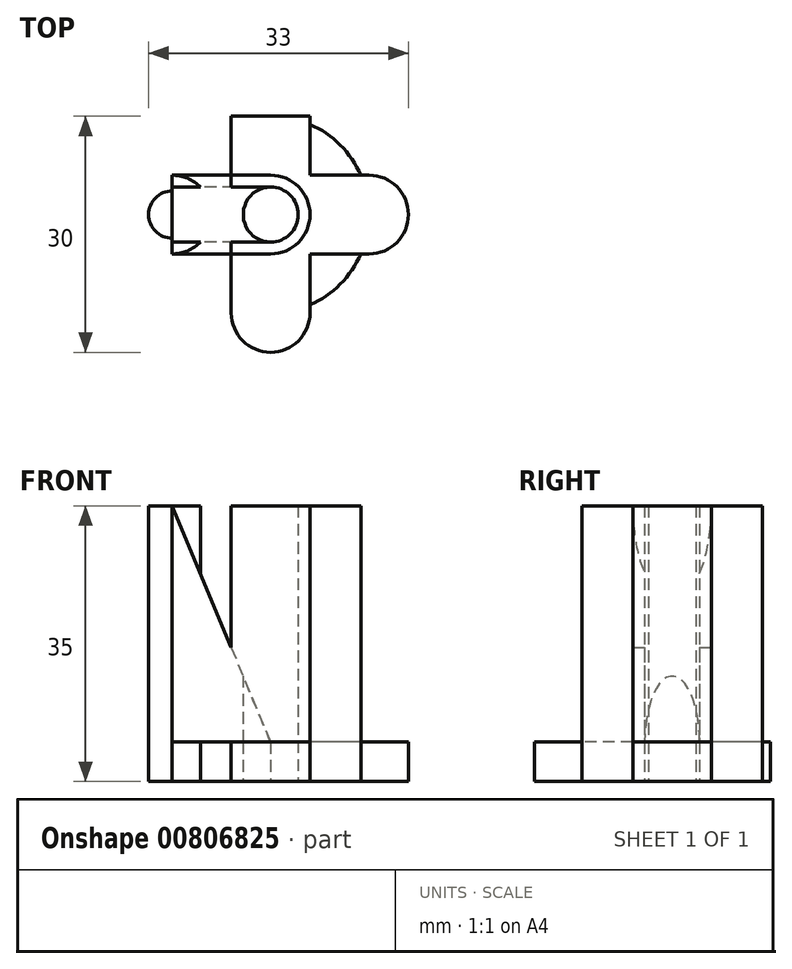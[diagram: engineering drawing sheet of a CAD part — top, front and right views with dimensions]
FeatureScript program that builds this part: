
annotation { "Feature Type Name" : "Feature", "Feature Type Description" : "" }
export const myFeature = defineFeature(function(context is Context, id is Id, definition is map)
    precondition{}
    {
        {
            var Q0;
            Q0=qCreatedBy(makeId("Top.planeOp"),FACE);
            var sketch = newSketch(context, id + "F0", { "sketchPlane" : qUnion([Q0])});
            skCircle(sketch, "E0", {"center": v(0, 0) * mm, "radius": 12.5 * mm});
            skCircle(sketch, "E1", {"center": v(0, 0) * mm, "radius": 3.5 * mm});
            skCircle(sketch, "E2", {"center": v(0, -12.5) * mm, "radius": 5 * mm});
            skCircle(sketch, "E3", {"center": v(0, 12.5) * mm, "radius": 5 * mm});
            skCircle(sketch, "E4", {"center": v(12.5, 0) * mm, "radius": 5 * mm});
            skCircle(sketch, "E5", {"center": v(-12.5, 0) * mm, "radius": 5 * mm});
            skCircle(sketch, "E6", {"center": v(-12.5, 0) * mm, "radius": 3 * mm});
            skCircle(sketch, "E7", {"center": v(0, 12.5) * mm, "radius": 3 * mm});
            skCircle(sketch, "E8", {"center": v(12.5, 0) * mm, "radius": 3 * mm});
            skCircle(sketch, "E9", {"center": v(0, -12.5) * mm, "radius": 3 * mm});
            skCircle(sketch, "E10", {"center": v(0, 0) * mm, "radius": 5 * mm});
            skLineSegment(sketch, "E11.bottom", {"start": v(0, 3.5) * mm, "end": v(-12.5, 3.5) * mm});
            skLineSegment(sketch, "E11.top", {"start": v(0, 5) * mm, "end": v(-12.5, 5) * mm});
            skLineSegment(sketch, "E11.left", {"start": v(0, 3.5) * mm, "end": v(0, 5) * mm});
            skLineSegment(sketch, "E11.right", {"start": v(-12.5, 3.5) * mm, "end": v(-12.5, 5) * mm});
            skLineSegment(sketch, "E12.bottom", {"start": v(0, -3.5) * mm, "end": v(-12.5, -3.5) * mm});
            skLineSegment(sketch, "E12.top", {"start": v(0, -5) * mm, "end": v(-12.5, -5) * mm});
            skLineSegment(sketch, "E12.left", {"start": v(0, -3.5) * mm, "end": v(0, -5) * mm});
            skLineSegment(sketch, "E12.right", {"start": v(-12.5, -3.5) * mm, "end": v(-12.5, -5) * mm});
            skLineSegment(sketch, "E13.bottom", {"start": v(5, 12.5) * mm, "end": v(-5, 12.5) * mm});
            skLineSegment(sketch, "E13.top", {"start": v(5, -12.5) * mm, "end": v(-5, -12.5) * mm});
            skLineSegment(sketch, "E13.left", {"start": v(5, 12.5) * mm, "end": v(5, -12.5) * mm});
            skLineSegment(sketch, "E13.right", {"start": v(-5, 12.5) * mm, "end": v(-5, -12.5) * mm});
            skLineSegment(sketch, "E14.bottom", {"start": v(12.5, 5) * mm, "end": v(-12.5, 5) * mm});
            skLineSegment(sketch, "E14.top", {"start": v(12.5, -5) * mm, "end": v(-12.5, -5) * mm});
            skLineSegment(sketch, "E14.left", {"start": v(12.5, 5) * mm, "end": v(12.5, -5) * mm});
            skLineSegment(sketch, "E14.right", {"start": v(-12.5, 5) * mm, "end": v(-12.5, -5) * mm});
            skSolve(sketch);
        }
        {
            var Q0;
            Q0=qCreatedBy(makeId("Front.planeOp"),FACE);
            var sketch = newSketch(context, id + "F1", { "sketchPlane" : qUnion([Q0])});
            skLineSegment(sketch, "E15", {"start": v(0, 0) * mm, "end": v(0, 10) * mm});
            skLineSegment(sketch, "E16", {"start": v(0, 10) * mm, "end": v(-12.5, 10) * mm});
            skLineSegment(sketch, "E17", {"start": v(-12.5, 10) * mm, "end": v(-12.5, 40) * mm});
            skLineSegment(sketch, "E18", {"start": v(-12.5, 40) * mm, "end": v(0, 10) * mm});
            skSolve(sketch);
        }
        {
            var Q0;
            Q0=makeQuery(id+"F1.imprint","IMPRINT",FACE,{"disambiguationData":[TD([[makeQuery(id+"F1.imprint","IMPRINT",EDGE,{"derivedFrom":sQuery(id+"F1.wireOp",EDGE,"E16")}),-1.0]])]});
            extrude(context, id + "F2", {"entities" : qUnion([Q0]), "endBound" : BoundingType.SYMMETRIC, "depth" : 10 * mm, "offsetDistance" : 25 * mm});
        }
        {
            var Q0;
            {var subQ0=sQuery(id+"F0.wireOp",EDGE,"E11.left");Q0=makeQuery(id+"F0.imprint","IMPRINT",FACE,{"disambiguationData":[TD([[makeQuery(id+"F0.imprint","IMPRINT",EDGE,{"derivedFrom":subQ0}),-1.0]])]});}
            var Q1;
            {var subQ0=sQuery(id+"F0.wireOp",EDGE,"E11.left");Q1=makeQuery(id+"F0.imprint","IMPRINT",FACE,{"disambiguationData":[TD([[makeQuery(id+"F0.imprint","IMPRINT",EDGE,{"derivedFrom":subQ0}),1.0]])]});}
            var Q2;
            {var subQ1=sQuery(id+"F0.wireOp",EDGE,"E10");var subQ3=sQuery(id+"F0.wireOp",EDGE,"E11.bottom");var subQ4=makeQuery(id+"F0.imprint","INTERSECT",VERTEX,{"derivedFrom":[subQ1,subQ3]});Q2=makeQuery(id+"F0.imprint","IMPRINT",FACE,{"disambiguationData":[TD([[makeQuery(id+"F0.imprint","IMPRINT",EDGE,{"disambiguationData":[TD([[subQ4,-1.0]])],"derivedFrom":subQ3}),-1.0]])]});}
            var Q3;
            {var subQ3=sQuery(id+"F0.wireOp",EDGE,"E14.bottom");var subQ7=sQuery(id+"F0.wireOp",EDGE,"E0");var subQ9=makeQuery(id+"F0.imprint","INTERSECT",VERTEX,{"disambiguationData":[OD(1.0)],"derivedFrom":[subQ7,subQ3]});Q3=makeQuery(id+"F0.imprint","IMPRINT",FACE,{"disambiguationData":[TD([[makeQuery(id+"F0.imprint","IMPRINT",EDGE,{"disambiguationData":[TD([[subQ9,-1.0]])],"derivedFrom":subQ7}),1.0]])]});}
            var Q4;
            {var subQ0=sQuery(id+"F0.wireOp",EDGE,"E5");var subQ1=sQuery(id+"F0.wireOp",EDGE,"E0");var subQ2=makeQuery(id+"F0.imprint","INTERSECT",VERTEX,{"disambiguationData":[OD(0.0)],"derivedFrom":[subQ1,subQ0]});Q4=makeQuery(id+"F0.imprint","IMPRINT",FACE,{"disambiguationData":[TD([[makeQuery(id+"F0.imprint","IMPRINT",EDGE,{"disambiguationData":[TD([[subQ2,-1.0]])],"derivedFrom":subQ1}),1.0]])]});}
            var Q5;
            {var subQ0=sQuery(id+"F0.wireOp",EDGE,"E5");var subQ1=sQuery(id+"F0.wireOp",EDGE,"E0");var subQ2=makeQuery(id+"F0.imprint","INTERSECT",VERTEX,{"disambiguationData":[OD(0.0)],"derivedFrom":[subQ1,subQ0]});Q5=makeQuery(id+"F0.imprint","IMPRINT",FACE,{"disambiguationData":[TD([[makeQuery(id+"F0.imprint","IMPRINT",EDGE,{"disambiguationData":[TD([[subQ2,-1.0]])],"derivedFrom":subQ1}),-1.0]])]});}
            var Q6;
            {var subQ0=sQuery(id+"F0.wireOp",EDGE,"E12.bottom");var subQ1=sQuery(id+"F0.wireOp",EDGE,"E0");var subQ2=makeQuery(id+"F0.imprint","INTERSECT",VERTEX,{"derivedFrom":[subQ1,subQ0]});Q6=makeQuery(id+"F0.imprint","IMPRINT",FACE,{"disambiguationData":[TD([[makeQuery(id+"F0.imprint","IMPRINT",EDGE,{"disambiguationData":[TD([[subQ2,-1.0]])],"derivedFrom":subQ1}),-1.0]])]});}
            var Q7;
            {var subQ0=sQuery(id+"F0.wireOp",EDGE,"E12.bottom");var subQ1=sQuery(id+"F0.wireOp",EDGE,"E0");var subQ2=makeQuery(id+"F0.imprint","INTERSECT",VERTEX,{"derivedFrom":[subQ1,subQ0]});Q7=makeQuery(id+"F0.imprint","IMPRINT",FACE,{"disambiguationData":[TD([[makeQuery(id+"F0.imprint","IMPRINT",EDGE,{"disambiguationData":[TD([[subQ2,-1.0]])],"derivedFrom":subQ1}),1.0]])]});}
            var Q8;
            {var subQ5=sQuery(id+"F0.wireOp",EDGE,"E14.top");var subQ7=sQuery(id+"F0.wireOp",EDGE,"E0");var subQ9=makeQuery(id+"F0.imprint","INTERSECT",VERTEX,{"disambiguationData":[OD(0.0)],"derivedFrom":[subQ7,subQ5]});Q8=makeQuery(id+"F0.imprint","IMPRINT",FACE,{"disambiguationData":[TD([[makeQuery(id+"F0.imprint","IMPRINT",EDGE,{"disambiguationData":[TD([[subQ9,1.0]])],"derivedFrom":subQ7}),1.0]])]});}
            var Q9;
            {var subQ1=sQuery(id+"F0.wireOp",EDGE,"E10");var subQ3=sQuery(id+"F0.wireOp",EDGE,"E12.bottom");var subQ4=makeQuery(id+"F0.imprint","INTERSECT",VERTEX,{"derivedFrom":[subQ1,subQ3]});Q9=makeQuery(id+"F0.imprint","IMPRINT",FACE,{"disambiguationData":[TD([[makeQuery(id+"F0.imprint","IMPRINT",EDGE,{"disambiguationData":[TD([[subQ4,-1.0]])],"derivedFrom":subQ3}),1.0]])]});}
            var Q10;
            {var subQ0=sQuery(id+"F0.wireOp",EDGE,"E12.left");Q10=makeQuery(id+"F0.imprint","IMPRINT",FACE,{"disambiguationData":[TD([[makeQuery(id+"F0.imprint","IMPRINT",EDGE,{"derivedFrom":subQ0}),-1.0]])]});}
            var Q11;
            {var subQ0=sQuery(id+"F0.wireOp",EDGE,"E14.top");var subQ1=sQuery(id+"F0.wireOp",EDGE,"E0");var subQ2=makeQuery(id+"F0.imprint","INTERSECT",VERTEX,{"disambiguationData":[OD(0.0)],"derivedFrom":[subQ1,subQ0]});Q11=makeQuery(id+"F0.imprint","IMPRINT",FACE,{"disambiguationData":[TD([[makeQuery(id+"F0.imprint","IMPRINT",EDGE,{"disambiguationData":[TD([[subQ2,1.0]])],"derivedFrom":subQ1}),-1.0]])]});}
            var Q12;
            {var subQ0=sQuery(id+"F0.wireOp",EDGE,"E14.bottom");var subQ1=sQuery(id+"F0.wireOp",EDGE,"E0");var subQ2=makeQuery(id+"F0.imprint","INTERSECT",VERTEX,{"disambiguationData":[OD(1.0)],"derivedFrom":[subQ1,subQ0]});Q12=makeQuery(id+"F0.imprint","IMPRINT",FACE,{"disambiguationData":[TD([[makeQuery(id+"F0.imprint","IMPRINT",EDGE,{"disambiguationData":[TD([[subQ2,-1.0]])],"derivedFrom":subQ1}),-1.0]])]});}
            var Q13;
            {var subQ0=sQuery(id+"F0.wireOp",EDGE,"E14.right");var subQ4=makeQuery(id+"F0.imprint","INTERSECT",VERTEX,{"derivedFrom":[sQuery(id+"F0.wireOp",EDGE,"E0"),subQ0]});Q13=makeQuery(id+"F0.imprint","IMPRINT",FACE,{"disambiguationData":[TD([[makeQuery(id+"F0.imprint","IMPRINT",EDGE,{"disambiguationData":[TD([[subQ4,1.0]])],"derivedFrom":subQ0}),-1.0]])]});}
            var Q14;
            {var subQ0=sQuery(id+"F0.wireOp",EDGE,"E14.right");var subQ1=sQuery(id+"F0.wireOp",EDGE,"E5");var subQ2=makeQuery(id+"F0.imprint","INTERSECT",VERTEX,{"derivedFrom":[subQ1,sQuery(id+"F0.wireOp",EDGE,"E14.bottom"),subQ0]});Q14=makeQuery(id+"F0.imprint","IMPRINT",FACE,{"disambiguationData":[TD([[makeQuery(id+"F0.imprint","IMPRINT",EDGE,{"disambiguationData":[TD([[subQ2,-1.0]])],"derivedFrom":subQ1}),1.0]])]});}
            extrude(context, id + "F3", {"entities" : qUnion([Q0, Q1, Q2, Q3, Q4, Q5, Q6, Q7, Q8, Q9, Q10, Q11, Q12, Q13, Q14]), "operationType" : NewBodyOperationType.ADD, "depth" : 40 * mm, "offsetDistance" : 25 * mm});
        }
        {
            var Q0;
            {var subQ0=sQuery(id+"F0.wireOp",EDGE,"E11.bottom");var subQ3=sQuery(id+"F0.wireOp",EDGE,"E10");var subQ4=makeQuery(id+"F0.imprint","INTERSECT",VERTEX,{"derivedFrom":[subQ3,subQ0]});Q0=makeQuery(id+"F0.imprint","IMPRINT",FACE,{"disambiguationData":[TD([[makeQuery(id+"F0.imprint","IMPRINT",EDGE,{"disambiguationData":[TD([[subQ4,-1.0]])],"derivedFrom":subQ3}),1.0]])]});}
            var Q1;
            {var subQ0=sQuery(id+"F0.wireOp",EDGE,"E11.bottom");var subQ1=sQuery(id+"F0.wireOp",EDGE,"E10");var subQ2=makeQuery(id+"F0.imprint","INTERSECT",VERTEX,{"derivedFrom":[subQ1,subQ0]});Q1=makeQuery(id+"F0.imprint","IMPRINT",FACE,{"disambiguationData":[TD([[makeQuery(id+"F0.imprint","IMPRINT",EDGE,{"disambiguationData":[TD([[subQ2,-1.0]])],"derivedFrom":subQ1}),-1.0]])]});}
            var Q2;
            {var subQ0=sQuery(id+"F0.wireOp",EDGE,"E13.right");var subQ1=sQuery(id+"F0.wireOp",EDGE,"E10");var subQ2=makeQuery(id+"F0.imprint","INTERSECT",VERTEX,{"derivedFrom":[subQ1,subQ0]});Q2=makeQuery(id+"F0.imprint","IMPRINT",FACE,{"disambiguationData":[TD([[makeQuery(id+"F0.imprint","IMPRINT",EDGE,{"disambiguationData":[TD([[subQ2,-1.0]])],"derivedFrom":subQ1}),-1.0]])]});}
            var Q3;
            {var subQ2=sQuery(id+"F0.wireOp",EDGE,"E11.bottom");var subQ5=sQuery(id+"F0.wireOp",EDGE,"E5");var subQ8=makeQuery(id+"F0.imprint","INTERSECT",VERTEX,{"derivedFrom":[subQ5,subQ2]});Q3=makeQuery(id+"F0.imprint","IMPRINT",FACE,{"disambiguationData":[TD([[makeQuery(id+"F0.imprint","IMPRINT",EDGE,{"disambiguationData":[TD([[subQ8,1.0]])],"derivedFrom":subQ5}),-1.0]])]});}
            var Q4;
            {var subQ0=sQuery(id+"F0.wireOp",EDGE,"E11.bottom");var subQ6=sQuery(id+"F0.wireOp",EDGE,"E0");var subQ10=makeQuery(id+"F0.imprint","INTERSECT",VERTEX,{"derivedFrom":[subQ6,subQ0]});Q4=makeQuery(id+"F0.imprint","IMPRINT",FACE,{"disambiguationData":[TD([[makeQuery(id+"F0.imprint","IMPRINT",EDGE,{"disambiguationData":[TD([[subQ10,-1.0]])],"derivedFrom":subQ6}),1.0]])]});}
            var Q5;
            {var subQ0=sQuery(id+"F0.wireOp",EDGE,"E6");var subQ1=sQuery(id+"F0.wireOp",EDGE,"E0");var subQ2=makeQuery(id+"F0.imprint","INTERSECT",VERTEX,{"disambiguationData":[OD(0.0)],"derivedFrom":[subQ1,subQ0]});Q5=makeQuery(id+"F0.imprint","IMPRINT",FACE,{"disambiguationData":[TD([[makeQuery(id+"F0.imprint","IMPRINT",EDGE,{"disambiguationData":[TD([[subQ2,-1.0]])],"derivedFrom":subQ1}),1.0]])]});}
            var Q6;
            {var subQ0=sQuery(id+"F0.wireOp",EDGE,"E6");var subQ1=sQuery(id+"F0.wireOp",EDGE,"E0");var subQ2=makeQuery(id+"F0.imprint","INTERSECT",VERTEX,{"disambiguationData":[OD(0.0)],"derivedFrom":[subQ1,subQ0]});Q6=makeQuery(id+"F0.imprint","IMPRINT",FACE,{"disambiguationData":[TD([[makeQuery(id+"F0.imprint","IMPRINT",EDGE,{"disambiguationData":[TD([[subQ2,-1.0]])],"derivedFrom":subQ1}),-1.0]])]});}
            var Q7;
            {var subQ0=sQuery(id+"F0.wireOp",EDGE,"E14.right");var subQ1=sQuery(id+"F0.wireOp",EDGE,"E0");var subQ2=makeQuery(id+"F0.imprint","INTERSECT",VERTEX,{"derivedFrom":[subQ1,subQ0]});Q7=makeQuery(id+"F0.imprint","IMPRINT",FACE,{"disambiguationData":[TD([[makeQuery(id+"F0.imprint","IMPRINT",EDGE,{"disambiguationData":[TD([[subQ2,-1.0]])],"derivedFrom":subQ1}),-1.0]])]});}
            var Q8;
            {var subQ0=sQuery(id+"F0.wireOp",EDGE,"E13.left");var subQ1=sQuery(id+"F0.wireOp",EDGE,"E0");var subQ2=makeQuery(id+"F0.imprint","INTERSECT",VERTEX,{"disambiguationData":[OD(0.0)],"derivedFrom":[subQ1,subQ0]});Q8=makeQuery(id+"F0.imprint","IMPRINT",FACE,{"disambiguationData":[TD([[makeQuery(id+"F0.imprint","IMPRINT",EDGE,{"disambiguationData":[TD([[subQ2,-1.0]])],"derivedFrom":subQ1}),1.0]])]});}
            var Q9;
            {var subQ0=sQuery(id+"F0.wireOp",EDGE,"E3");var subQ1=sQuery(id+"F0.wireOp",EDGE,"E0");var subQ2=makeQuery(id+"F0.imprint","INTERSECT",VERTEX,{"disambiguationData":[OD(0.0)],"derivedFrom":[subQ1,subQ0]});Q9=makeQuery(id+"F0.imprint","IMPRINT",FACE,{"disambiguationData":[TD([[makeQuery(id+"F0.imprint","IMPRINT",EDGE,{"disambiguationData":[TD([[subQ2,-1.0]])],"derivedFrom":subQ1}),1.0]])]});}
            var Q10;
            {var subQ0=sQuery(id+"F0.wireOp",EDGE,"E7");var subQ1=sQuery(id+"F0.wireOp",EDGE,"E0");var subQ2=makeQuery(id+"F0.imprint","INTERSECT",VERTEX,{"disambiguationData":[OD(0.0)],"derivedFrom":[subQ1,subQ0]});Q10=makeQuery(id+"F0.imprint","IMPRINT",FACE,{"disambiguationData":[TD([[makeQuery(id+"F0.imprint","IMPRINT",EDGE,{"disambiguationData":[TD([[subQ2,-1.0]])],"derivedFrom":subQ1}),1.0]])]});}
            var Q11;
            {var subQ0=sQuery(id+"F0.wireOp",EDGE,"E7");var subQ1=sQuery(id+"F0.wireOp",EDGE,"E0");var subQ2=makeQuery(id+"F0.imprint","INTERSECT",VERTEX,{"disambiguationData":[OD(0.0)],"derivedFrom":[subQ1,subQ0]});Q11=makeQuery(id+"F0.imprint","IMPRINT",FACE,{"disambiguationData":[TD([[makeQuery(id+"F0.imprint","IMPRINT",EDGE,{"disambiguationData":[TD([[subQ2,-1.0]])],"derivedFrom":subQ1}),-1.0]])]});}
            var Q12;
            {var subQ0=sQuery(id+"F0.wireOp",EDGE,"E3");var subQ1=sQuery(id+"F0.wireOp",EDGE,"E0");var subQ2=makeQuery(id+"F0.imprint","INTERSECT",VERTEX,{"disambiguationData":[OD(0.0)],"derivedFrom":[subQ1,subQ0]});Q12=makeQuery(id+"F0.imprint","IMPRINT",FACE,{"disambiguationData":[TD([[makeQuery(id+"F0.imprint","IMPRINT",EDGE,{"disambiguationData":[TD([[subQ2,-1.0]])],"derivedFrom":subQ1}),-1.0]])]});}
            var Q13;
            {var subQ0=sQuery(id+"F0.wireOp",EDGE,"E13.bottom");var subQ4=sQuery(id+"F0.wireOp",EDGE,"E7");var subQ5=makeQuery(id+"F0.imprint","INTERSECT",VERTEX,{"disambiguationData":[OD(0.0)],"derivedFrom":[subQ4,subQ0]});Q13=makeQuery(id+"F0.imprint","IMPRINT",FACE,{"disambiguationData":[TD([[makeQuery(id+"F0.imprint","IMPRINT",EDGE,{"disambiguationData":[TD([[subQ5,1.0]])],"derivedFrom":subQ4}),-1.0]])]});}
            var Q14;
            {var subQ0=sQuery(id+"F0.wireOp",EDGE,"E13.bottom");var subQ1=sQuery(id+"F0.wireOp",EDGE,"E7");var subQ2=makeQuery(id+"F0.imprint","INTERSECT",VERTEX,{"disambiguationData":[OD(0.0)],"derivedFrom":[subQ1,subQ0]});Q14=makeQuery(id+"F0.imprint","IMPRINT",FACE,{"disambiguationData":[TD([[makeQuery(id+"F0.imprint","IMPRINT",EDGE,{"disambiguationData":[TD([[subQ2,1.0]])],"derivedFrom":subQ1}),1.0]])]});}
            var Q15;
            {var subQ0=sQuery(id+"F0.wireOp",EDGE,"E13.bottom");var subQ1=sQuery(id+"F0.wireOp",EDGE,"E0");var subQ2=makeQuery(id+"F0.imprint","INTERSECT",VERTEX,{"derivedFrom":[subQ1,subQ0]});Q15=makeQuery(id+"F0.imprint","IMPRINT",FACE,{"disambiguationData":[TD([[makeQuery(id+"F0.imprint","IMPRINT",EDGE,{"disambiguationData":[TD([[subQ2,-1.0]])],"derivedFrom":subQ1}),-1.0]])]});}
            var Q16;
            {var subQ0=sQuery(id+"F0.wireOp",EDGE,"E7");var subQ1=sQuery(id+"F0.wireOp",EDGE,"E0");var subQ2=makeQuery(id+"F0.imprint","INTERSECT",VERTEX,{"disambiguationData":[OD(1.0)],"derivedFrom":[subQ1,subQ0]});Q16=makeQuery(id+"F0.imprint","IMPRINT",FACE,{"disambiguationData":[TD([[makeQuery(id+"F0.imprint","IMPRINT",EDGE,{"disambiguationData":[TD([[subQ2,-1.0]])],"derivedFrom":subQ1}),-1.0]])]});}
            var Q17;
            {var subQ0=sQuery(id+"F0.wireOp",EDGE,"E8");var subQ1=sQuery(id+"F0.wireOp",EDGE,"E0");var subQ2=makeQuery(id+"F0.imprint","INTERSECT",VERTEX,{"disambiguationData":[OD(0.0)],"derivedFrom":[subQ1,subQ0]});Q17=makeQuery(id+"F0.imprint","IMPRINT",FACE,{"disambiguationData":[TD([[makeQuery(id+"F0.imprint","IMPRINT",EDGE,{"disambiguationData":[TD([[subQ2,-1.0]])],"derivedFrom":subQ1}),1.0]])]});}
            var Q18;
            {var subQ0=sQuery(id+"F0.wireOp",EDGE,"E8");var subQ1=sQuery(id+"F0.wireOp",EDGE,"E0");var subQ2=makeQuery(id+"F0.imprint","INTERSECT",VERTEX,{"disambiguationData":[OD(0.0)],"derivedFrom":[subQ1,subQ0]});Q18=makeQuery(id+"F0.imprint","IMPRINT",FACE,{"disambiguationData":[TD([[makeQuery(id+"F0.imprint","IMPRINT",EDGE,{"disambiguationData":[TD([[subQ2,-1.0]])],"derivedFrom":subQ1}),-1.0]])]});}
            var Q19;
            {var subQ0=sQuery(id+"F0.wireOp",EDGE,"E14.left");var subQ4=sQuery(id+"F0.wireOp",EDGE,"E8");var subQ5=makeQuery(id+"F0.imprint","INTERSECT",VERTEX,{"disambiguationData":[OD(0.0)],"derivedFrom":[subQ4,subQ0]});Q19=makeQuery(id+"F0.imprint","IMPRINT",FACE,{"disambiguationData":[TD([[makeQuery(id+"F0.imprint","IMPRINT",EDGE,{"disambiguationData":[TD([[subQ5,1.0]])],"derivedFrom":subQ4}),-1.0]])]});}
            var Q20;
            {var subQ0=sQuery(id+"F0.wireOp",EDGE,"E14.left");var subQ1=sQuery(id+"F0.wireOp",EDGE,"E8");var subQ2=makeQuery(id+"F0.imprint","INTERSECT",VERTEX,{"disambiguationData":[OD(0.0)],"derivedFrom":[subQ1,subQ0]});Q20=makeQuery(id+"F0.imprint","IMPRINT",FACE,{"disambiguationData":[TD([[makeQuery(id+"F0.imprint","IMPRINT",EDGE,{"disambiguationData":[TD([[subQ2,1.0]])],"derivedFrom":subQ1}),1.0]])]});}
            var Q21;
            {var subQ0=sQuery(id+"F0.wireOp",EDGE,"E8");var subQ1=sQuery(id+"F0.wireOp",EDGE,"E0");var subQ2=makeQuery(id+"F0.imprint","INTERSECT",VERTEX,{"disambiguationData":[OD(0.0)],"derivedFrom":[subQ1,subQ0]});Q21=makeQuery(id+"F0.imprint","IMPRINT",FACE,{"disambiguationData":[TD([[makeQuery(id+"F0.imprint","IMPRINT",EDGE,{"disambiguationData":[TD([[subQ2,1.0]])],"derivedFrom":subQ1}),1.0]])]});}
            var Q22;
            {var subQ0=sQuery(id+"F0.wireOp",EDGE,"E8");var subQ1=sQuery(id+"F0.wireOp",EDGE,"E0");var subQ2=makeQuery(id+"F0.imprint","INTERSECT",VERTEX,{"disambiguationData":[OD(0.0)],"derivedFrom":[subQ1,subQ0]});Q22=makeQuery(id+"F0.imprint","IMPRINT",FACE,{"disambiguationData":[TD([[makeQuery(id+"F0.imprint","IMPRINT",EDGE,{"disambiguationData":[TD([[subQ2,1.0]])],"derivedFrom":subQ1}),-1.0]])]});}
            var Q23;
            {var subQ0=sQuery(id+"F0.wireOp",EDGE,"E14.left");var subQ1=sQuery(id+"F0.wireOp",EDGE,"E0");var subQ2=makeQuery(id+"F0.imprint","INTERSECT",VERTEX,{"derivedFrom":[subQ1,subQ0]});Q23=makeQuery(id+"F0.imprint","IMPRINT",FACE,{"disambiguationData":[TD([[makeQuery(id+"F0.imprint","IMPRINT",EDGE,{"disambiguationData":[TD([[subQ2,1.0]])],"derivedFrom":subQ1}),-1.0]])]});}
            var Q24;
            {var subQ0=sQuery(id+"F0.wireOp",EDGE,"E4");var subQ1=sQuery(id+"F0.wireOp",EDGE,"E0");var subQ2=makeQuery(id+"F0.imprint","INTERSECT",VERTEX,{"disambiguationData":[OD(1.0)],"derivedFrom":[subQ1,subQ0]});Q24=makeQuery(id+"F0.imprint","IMPRINT",FACE,{"disambiguationData":[TD([[makeQuery(id+"F0.imprint","IMPRINT",EDGE,{"disambiguationData":[TD([[subQ2,-1.0]])],"derivedFrom":subQ1}),-1.0]])]});}
            var Q25;
            {var subQ2=sQuery(id+"F0.wireOp",EDGE,"E14.bottom");var subQ5=sQuery(id+"F0.wireOp",EDGE,"E0");var subQ8=makeQuery(id+"F0.imprint","INTERSECT",VERTEX,{"disambiguationData":[OD(0.0)],"derivedFrom":[subQ5,subQ2]});Q25=makeQuery(id+"F0.imprint","IMPRINT",FACE,{"disambiguationData":[TD([[makeQuery(id+"F0.imprint","IMPRINT",EDGE,{"disambiguationData":[TD([[subQ8,1.0]])],"derivedFrom":subQ5}),1.0]])]});}
            var Q26;
            {var subQ0=sQuery(id+"F0.wireOp",EDGE,"E13.left");var subQ1=sQuery(id+"F0.wireOp",EDGE,"E0");var subQ2=makeQuery(id+"F0.imprint","INTERSECT",VERTEX,{"disambiguationData":[OD(0.0)],"derivedFrom":[subQ1,subQ0]});Q26=makeQuery(id+"F0.imprint","IMPRINT",FACE,{"disambiguationData":[TD([[makeQuery(id+"F0.imprint","IMPRINT",EDGE,{"disambiguationData":[TD([[subQ2,-1.0]])],"derivedFrom":subQ1}),-1.0]])]});}
            var Q27;
            {var subQ0=sQuery(id+"F0.wireOp",EDGE,"E13.right");var subQ1=sQuery(id+"F0.wireOp",EDGE,"E0");var subQ2=makeQuery(id+"F0.imprint","INTERSECT",VERTEX,{"disambiguationData":[OD(0.0)],"derivedFrom":[subQ1,subQ0]});Q27=makeQuery(id+"F0.imprint","IMPRINT",FACE,{"disambiguationData":[TD([[makeQuery(id+"F0.imprint","IMPRINT",EDGE,{"disambiguationData":[TD([[subQ2,1.0]])],"derivedFrom":subQ1}),-1.0]])]});}
            var Q28;
            {var subQ0=sQuery(id+"F0.wireOp",EDGE,"E14.bottom");var subQ1=sQuery(id+"F0.wireOp",EDGE,"E0");var subQ2=makeQuery(id+"F0.imprint","INTERSECT",VERTEX,{"disambiguationData":[OD(0.0)],"derivedFrom":[subQ1,subQ0]});Q28=makeQuery(id+"F0.imprint","IMPRINT",FACE,{"disambiguationData":[TD([[makeQuery(id+"F0.imprint","IMPRINT",EDGE,{"disambiguationData":[TD([[subQ2,1.0]])],"derivedFrom":subQ1}),-1.0]])]});}
            var Q29;
            {var subQ0=sQuery(id+"F0.wireOp",EDGE,"E14.top");var subQ1=sQuery(id+"F0.wireOp",EDGE,"E0");var subQ2=makeQuery(id+"F0.imprint","INTERSECT",VERTEX,{"disambiguationData":[OD(1.0)],"derivedFrom":[subQ1,subQ0]});Q29=makeQuery(id+"F0.imprint","IMPRINT",FACE,{"disambiguationData":[TD([[makeQuery(id+"F0.imprint","IMPRINT",EDGE,{"disambiguationData":[TD([[subQ2,-1.0]])],"derivedFrom":subQ1}),-1.0]])]});}
            var Q30;
            {var subQ0=sQuery(id+"F0.wireOp",EDGE,"E13.top");var subQ4=sQuery(id+"F0.wireOp",EDGE,"E9");var subQ5=makeQuery(id+"F0.imprint","INTERSECT",VERTEX,{"disambiguationData":[OD(0.0)],"derivedFrom":[subQ4,subQ0]});Q30=makeQuery(id+"F0.imprint","IMPRINT",FACE,{"disambiguationData":[TD([[makeQuery(id+"F0.imprint","IMPRINT",EDGE,{"disambiguationData":[TD([[subQ5,1.0]])],"derivedFrom":subQ4}),-1.0]])]});}
            var Q31;
            {var subQ0=sQuery(id+"F0.wireOp",EDGE,"E13.top");var subQ1=sQuery(id+"F0.wireOp",EDGE,"E0");var subQ2=makeQuery(id+"F0.imprint","INTERSECT",VERTEX,{"derivedFrom":[subQ1,subQ0]});Q31=makeQuery(id+"F0.imprint","IMPRINT",FACE,{"disambiguationData":[TD([[makeQuery(id+"F0.imprint","IMPRINT",EDGE,{"disambiguationData":[TD([[subQ2,-1.0]])],"derivedFrom":subQ1}),-1.0]])]});}
            var Q32;
            {var subQ0=sQuery(id+"F0.wireOp",EDGE,"E9");var subQ1=sQuery(id+"F0.wireOp",EDGE,"E0");var subQ2=makeQuery(id+"F0.imprint","INTERSECT",VERTEX,{"disambiguationData":[OD(1.0)],"derivedFrom":[subQ1,subQ0]});Q32=makeQuery(id+"F0.imprint","IMPRINT",FACE,{"disambiguationData":[TD([[makeQuery(id+"F0.imprint","IMPRINT",EDGE,{"disambiguationData":[TD([[subQ2,-1.0]])],"derivedFrom":subQ1}),-1.0]])]});}
            var Q33;
            {var subQ0=sQuery(id+"F0.wireOp",EDGE,"E13.top");var subQ1=sQuery(id+"F0.wireOp",EDGE,"E9");var subQ2=makeQuery(id+"F0.imprint","INTERSECT",VERTEX,{"disambiguationData":[OD(0.0)],"derivedFrom":[subQ1,subQ0]});Q33=makeQuery(id+"F0.imprint","IMPRINT",FACE,{"disambiguationData":[TD([[makeQuery(id+"F0.imprint","IMPRINT",EDGE,{"disambiguationData":[TD([[subQ2,1.0]])],"derivedFrom":subQ1}),1.0]])]});}
            var Q34;
            {var subQ0=sQuery(id+"F0.wireOp",EDGE,"E9");var subQ1=sQuery(id+"F0.wireOp",EDGE,"E0");var subQ2=makeQuery(id+"F0.imprint","INTERSECT",VERTEX,{"disambiguationData":[OD(0.0)],"derivedFrom":[subQ1,subQ0]});Q34=makeQuery(id+"F0.imprint","IMPRINT",FACE,{"disambiguationData":[TD([[makeQuery(id+"F0.imprint","IMPRINT",EDGE,{"disambiguationData":[TD([[subQ2,-1.0]])],"derivedFrom":subQ1}),1.0]])]});}
            var Q35;
            {var subQ0=sQuery(id+"F0.wireOp",EDGE,"E2");var subQ1=sQuery(id+"F0.wireOp",EDGE,"E0");var subQ2=makeQuery(id+"F0.imprint","INTERSECT",VERTEX,{"disambiguationData":[OD(0.0)],"derivedFrom":[subQ1,subQ0]});Q35=makeQuery(id+"F0.imprint","IMPRINT",FACE,{"disambiguationData":[TD([[makeQuery(id+"F0.imprint","IMPRINT",EDGE,{"disambiguationData":[TD([[subQ2,-1.0]])],"derivedFrom":subQ1}),1.0]])]});}
            var Q36;
            {var subQ0=sQuery(id+"F0.wireOp",EDGE,"E2");var subQ1=sQuery(id+"F0.wireOp",EDGE,"E0");var subQ2=makeQuery(id+"F0.imprint","INTERSECT",VERTEX,{"disambiguationData":[OD(0.0)],"derivedFrom":[subQ1,subQ0]});Q36=makeQuery(id+"F0.imprint","IMPRINT",FACE,{"disambiguationData":[TD([[makeQuery(id+"F0.imprint","IMPRINT",EDGE,{"disambiguationData":[TD([[subQ2,-1.0]])],"derivedFrom":subQ1}),-1.0]])]});}
            var Q37;
            {var subQ0=sQuery(id+"F0.wireOp",EDGE,"E9");var subQ1=sQuery(id+"F0.wireOp",EDGE,"E0");var subQ2=makeQuery(id+"F0.imprint","INTERSECT",VERTEX,{"disambiguationData":[OD(0.0)],"derivedFrom":[subQ1,subQ0]});Q37=makeQuery(id+"F0.imprint","IMPRINT",FACE,{"disambiguationData":[TD([[makeQuery(id+"F0.imprint","IMPRINT",EDGE,{"disambiguationData":[TD([[subQ2,-1.0]])],"derivedFrom":subQ1}),-1.0]])]});}
            var Q38;
            {var subQ1=sQuery(id+"F0.wireOp",EDGE,"E0");var subQ8=sQuery(id+"F0.wireOp",EDGE,"E13.right");var subQ9=makeQuery(id+"F0.imprint","INTERSECT",VERTEX,{"disambiguationData":[OD(1.0)],"derivedFrom":[subQ1,subQ8]});Q38=makeQuery(id+"F0.imprint","IMPRINT",FACE,{"disambiguationData":[TD([[makeQuery(id+"F0.imprint","IMPRINT",EDGE,{"disambiguationData":[TD([[subQ9,-1.0]])],"derivedFrom":subQ1}),1.0]])]});}
            var Q39;
            {var subQ0=sQuery(id+"F0.wireOp",EDGE,"E13.left");var subQ1=sQuery(id+"F0.wireOp",EDGE,"E0");var subQ2=makeQuery(id+"F0.imprint","INTERSECT",VERTEX,{"disambiguationData":[OD(1.0)],"derivedFrom":[subQ1,subQ0]});Q39=makeQuery(id+"F0.imprint","IMPRINT",FACE,{"disambiguationData":[TD([[makeQuery(id+"F0.imprint","IMPRINT",EDGE,{"disambiguationData":[TD([[subQ2,1.0]])],"derivedFrom":subQ1}),-1.0]])]});}
            var Q40;
            {var subQ0=sQuery(id+"F0.wireOp",EDGE,"E13.right");var subQ1=sQuery(id+"F0.wireOp",EDGE,"E0");var subQ2=makeQuery(id+"F0.imprint","INTERSECT",VERTEX,{"disambiguationData":[OD(1.0)],"derivedFrom":[subQ1,subQ0]});Q40=makeQuery(id+"F0.imprint","IMPRINT",FACE,{"disambiguationData":[TD([[makeQuery(id+"F0.imprint","IMPRINT",EDGE,{"disambiguationData":[TD([[subQ2,-1.0]])],"derivedFrom":subQ1}),-1.0]])]});}
            var Q41;
            {var subQ1=sQuery(id+"F0.wireOp",EDGE,"E10");var subQ3=sQuery(id+"F0.wireOp",EDGE,"E13.left");var subQ4=makeQuery(id+"F0.imprint","INTERSECT",VERTEX,{"derivedFrom":[subQ1,subQ3]});Q41=makeQuery(id+"F0.imprint","IMPRINT",FACE,{"disambiguationData":[TD([[makeQuery(id+"F0.imprint","IMPRINT",EDGE,{"disambiguationData":[TD([[subQ4,1.0]])],"derivedFrom":subQ3}),-1.0]])]});}
            var Q42;
            {var subQ1=sQuery(id+"F0.wireOp",EDGE,"E10");var subQ3=sQuery(id+"F0.wireOp",EDGE,"E13.left");var subQ4=makeQuery(id+"F0.imprint","INTERSECT",VERTEX,{"derivedFrom":[subQ1,subQ3]});Q42=makeQuery(id+"F0.imprint","IMPRINT",FACE,{"disambiguationData":[TD([[makeQuery(id+"F0.imprint","IMPRINT",EDGE,{"disambiguationData":[TD([[subQ4,-1.0]])],"derivedFrom":subQ3}),-1.0]])]});}
            var Q43;
            {var subQ0=sQuery(id+"F0.wireOp",EDGE,"E6");var subQ1=sQuery(id+"F0.wireOp",EDGE,"E0");var subQ2=makeQuery(id+"F0.imprint","INTERSECT",VERTEX,{"disambiguationData":[OD(1.0)],"derivedFrom":[subQ1,subQ0]});Q43=makeQuery(id+"F0.imprint","IMPRINT",FACE,{"disambiguationData":[TD([[makeQuery(id+"F0.imprint","IMPRINT",EDGE,{"disambiguationData":[TD([[subQ2,-1.0]])],"derivedFrom":subQ1}),-1.0]])]});}
            var Q44;
            {var subQ0=sQuery(id+"F0.wireOp",EDGE,"E11.bottom");var subQ1=sQuery(id+"F0.wireOp",EDGE,"E0");var subQ2=makeQuery(id+"F0.imprint","INTERSECT",VERTEX,{"derivedFrom":[subQ1,subQ0]});Q44=makeQuery(id+"F0.imprint","IMPRINT",FACE,{"disambiguationData":[TD([[makeQuery(id+"F0.imprint","IMPRINT",EDGE,{"disambiguationData":[TD([[subQ2,-1.0]])],"derivedFrom":subQ1}),-1.0]])]});}
            extrude(context, id + "F4", {"entities" : qUnion([Q0, Q1, Q2, Q3, Q4, Q5, Q6, Q7, Q8, Q9, Q10, Q11, Q12, Q13, Q14, Q15, Q16, Q17, Q18, Q19, Q20, Q21, Q22, Q23, Q24, Q25, Q26, Q27, Q28, Q29, Q30, Q31, Q32, Q33, Q34, Q35, Q36, Q37, Q38, Q39, Q40, Q41, Q42, Q43, Q44]), "depth" : 10 * mm, "offsetDistance" : 25 * mm});
        }
        {
            var Q0;
            {var subQ0=sQuery(id+"F0.wireOp",EDGE,"E1");var subQ1=makeQuery(id+"F0.imprint","INTERSECT",VERTEX,{"derivedFrom":[subQ0,sQuery(id+"F0.wireOp",EDGE,"E11.bottom"),sQuery(id+"F0.wireOp",EDGE,"E11.left")]});Q0=makeQuery(id+"F0.imprint","IMPRINT",FACE,{"disambiguationData":[TD([[makeQuery(id+"F0.imprint","IMPRINT",EDGE,{"disambiguationData":[TD([[subQ1,-1.0]])],"derivedFrom":subQ0}),1.0]])]});}
            extrude(context, id + "F5", {"entities" : qUnion([Q0]), "operationType" : NewBodyOperationType.REMOVE, "oppositeDirection" : true, "depth" : -40 * mm, "offsetDistance" : 25 * mm});
        }
        {
            var Q0;
            {var subQ0=sQuery(id+"F0.wireOp",EDGE,"E14.right");var subQ1=sQuery(id+"F0.wireOp",EDGE,"E5");var subQ2=makeQuery(id+"F0.imprint","INTERSECT",VERTEX,{"derivedFrom":[subQ1,sQuery(id+"F0.wireOp",EDGE,"E14.bottom"),subQ0]});Q0=makeQuery(id+"F0.imprint","IMPRINT",FACE,{"disambiguationData":[TD([[makeQuery(id+"F0.imprint","IMPRINT",EDGE,{"disambiguationData":[TD([[subQ2,-1.0]])],"derivedFrom":subQ1}),1.0]])]});}
            var Q1;
            {var subQ0=sQuery(id+"F0.wireOp",EDGE,"E13.bottom");var subQ4=sQuery(id+"F0.wireOp",EDGE,"E7");var subQ5=makeQuery(id+"F0.imprint","INTERSECT",VERTEX,{"disambiguationData":[OD(0.0)],"derivedFrom":[subQ4,subQ0]});Q1=makeQuery(id+"F0.imprint","IMPRINT",FACE,{"disambiguationData":[TD([[makeQuery(id+"F0.imprint","IMPRINT",EDGE,{"disambiguationData":[TD([[subQ5,1.0]])],"derivedFrom":subQ4}),-1.0]])]});}
            extrude(context, id + "F6", {"entities" : qUnion([Q0, Q1]), "oppositeDirection" : true, "depth" : 15 * mm, "offsetDistance" : 25 * mm});
        }
        {
            var Q0;
            {var subQ0=sQuery(id+"F0.wireOp",EDGE,"E14.right");var subQ4=makeQuery(id+"F0.imprint","INTERSECT",VERTEX,{"derivedFrom":[sQuery(id+"F0.wireOp",EDGE,"E0"),subQ0]});Q0=makeQuery(id+"F0.imprint","IMPRINT",FACE,{"disambiguationData":[TD([[makeQuery(id+"F0.imprint","IMPRINT",EDGE,{"disambiguationData":[TD([[subQ4,1.0]])],"derivedFrom":subQ0}),-1.0]])]});}
            var Q1;
            {var subQ0=sQuery(id+"F0.wireOp",EDGE,"E14.right");var subQ1=sQuery(id+"F0.wireOp",EDGE,"E0");var subQ2=makeQuery(id+"F0.imprint","INTERSECT",VERTEX,{"derivedFrom":[subQ1,subQ0]});Q1=makeQuery(id+"F0.imprint","IMPRINT",FACE,{"disambiguationData":[TD([[makeQuery(id+"F0.imprint","IMPRINT",EDGE,{"disambiguationData":[TD([[subQ2,-1.0]])],"derivedFrom":subQ1}),-1.0]])]});}
            var Q2;
            {var subQ0=sQuery(id+"F0.wireOp",EDGE,"E6");var subQ1=sQuery(id+"F0.wireOp",EDGE,"E0");var subQ2=makeQuery(id+"F0.imprint","INTERSECT",VERTEX,{"disambiguationData":[OD(0.0)],"derivedFrom":[subQ1,subQ0]});Q2=makeQuery(id+"F0.imprint","IMPRINT",FACE,{"disambiguationData":[TD([[makeQuery(id+"F0.imprint","IMPRINT",EDGE,{"disambiguationData":[TD([[subQ2,-1.0]])],"derivedFrom":subQ1}),1.0]])]});}
            var Q3;
            {var subQ0=sQuery(id+"F0.wireOp",EDGE,"E6");var subQ1=sQuery(id+"F0.wireOp",EDGE,"E0");var subQ2=makeQuery(id+"F0.imprint","INTERSECT",VERTEX,{"disambiguationData":[OD(0.0)],"derivedFrom":[subQ1,subQ0]});Q3=makeQuery(id+"F0.imprint","IMPRINT",FACE,{"disambiguationData":[TD([[makeQuery(id+"F0.imprint","IMPRINT",EDGE,{"disambiguationData":[TD([[subQ2,-1.0]])],"derivedFrom":subQ1}),-1.0]])]});}
            var Q4;
            {var subQ0=sQuery(id+"F0.wireOp",EDGE,"E7");var subQ1=sQuery(id+"F0.wireOp",EDGE,"E0");var subQ2=makeQuery(id+"F0.imprint","INTERSECT",VERTEX,{"disambiguationData":[OD(0.0)],"derivedFrom":[subQ1,subQ0]});Q4=makeQuery(id+"F0.imprint","IMPRINT",FACE,{"disambiguationData":[TD([[makeQuery(id+"F0.imprint","IMPRINT",EDGE,{"disambiguationData":[TD([[subQ2,-1.0]])],"derivedFrom":subQ1}),1.0]])]});}
            var Q5;
            {var subQ0=sQuery(id+"F0.wireOp",EDGE,"E7");var subQ1=sQuery(id+"F0.wireOp",EDGE,"E0");var subQ2=makeQuery(id+"F0.imprint","INTERSECT",VERTEX,{"disambiguationData":[OD(0.0)],"derivedFrom":[subQ1,subQ0]});Q5=makeQuery(id+"F0.imprint","IMPRINT",FACE,{"disambiguationData":[TD([[makeQuery(id+"F0.imprint","IMPRINT",EDGE,{"disambiguationData":[TD([[subQ2,-1.0]])],"derivedFrom":subQ1}),-1.0]])]});}
            var Q6;
            {var subQ0=sQuery(id+"F0.wireOp",EDGE,"E13.bottom");var subQ1=sQuery(id+"F0.wireOp",EDGE,"E0");var subQ2=makeQuery(id+"F0.imprint","INTERSECT",VERTEX,{"derivedFrom":[subQ1,subQ0]});Q6=makeQuery(id+"F0.imprint","IMPRINT",FACE,{"disambiguationData":[TD([[makeQuery(id+"F0.imprint","IMPRINT",EDGE,{"disambiguationData":[TD([[subQ2,-1.0]])],"derivedFrom":subQ1}),-1.0]])]});}
            var Q7;
            {var subQ0=sQuery(id+"F0.wireOp",EDGE,"E13.bottom");var subQ1=sQuery(id+"F0.wireOp",EDGE,"E7");var subQ2=makeQuery(id+"F0.imprint","INTERSECT",VERTEX,{"disambiguationData":[OD(0.0)],"derivedFrom":[subQ1,subQ0]});Q7=makeQuery(id+"F0.imprint","IMPRINT",FACE,{"disambiguationData":[TD([[makeQuery(id+"F0.imprint","IMPRINT",EDGE,{"disambiguationData":[TD([[subQ2,1.0]])],"derivedFrom":subQ1}),1.0]])]});}
            extrude(context, id + "F7", {"entities" : qUnion([Q0, Q1, Q2, Q3, Q4, Q5, Q6, Q7]), "oppositeDirection" : true, "depth" : 18 * mm, "offsetDistance" : 25 * mm});
        }
        {
            var Q0;
            Q0=makeQuery(id+"F7.opExtrude","CAP_FACE",FACE,{"disambiguationData":[OSD([sQuery(id+"F0.wireOp",EDGE,"E6")])],"isStart":false});
            var Q1;
            Q1=makeQuery(id+"F7.opExtrude","CAP_FACE",FACE,{"disambiguationData":[OSD([sQuery(id+"F0.wireOp",EDGE,"E7")])],"isStart":false});
            chamfer(context, id + "F8", {"entities" : qUnion([Q0, Q1]), "width" : 2 * mm, "tangentPropagation" : true});
        }
        {
            var Q0;
            {var subQ0=sQuery(id+"F0.wireOp",EDGE,"E14.left");var subQ1=sQuery(id+"F0.wireOp",EDGE,"E0");var subQ2=makeQuery(id+"F0.imprint","INTERSECT",VERTEX,{"derivedFrom":[subQ1,subQ0]});Q0=makeQuery(id+"F0.imprint","IMPRINT",FACE,{"disambiguationData":[TD([[makeQuery(id+"F0.imprint","IMPRINT",EDGE,{"disambiguationData":[TD([[subQ2,1.0]])],"derivedFrom":subQ1}),-1.0]])]});}
            var Q1;
            {var subQ0=sQuery(id+"F0.wireOp",EDGE,"E8");var subQ1=sQuery(id+"F0.wireOp",EDGE,"E0");var subQ2=makeQuery(id+"F0.imprint","INTERSECT",VERTEX,{"disambiguationData":[OD(0.0)],"derivedFrom":[subQ1,subQ0]});Q1=makeQuery(id+"F0.imprint","IMPRINT",FACE,{"disambiguationData":[TD([[makeQuery(id+"F0.imprint","IMPRINT",EDGE,{"disambiguationData":[TD([[subQ2,1.0]])],"derivedFrom":subQ1}),1.0]])]});}
            var Q2;
            {var subQ0=sQuery(id+"F0.wireOp",EDGE,"E8");var subQ1=sQuery(id+"F0.wireOp",EDGE,"E0");var subQ2=makeQuery(id+"F0.imprint","INTERSECT",VERTEX,{"disambiguationData":[OD(0.0)],"derivedFrom":[subQ1,subQ0]});Q2=makeQuery(id+"F0.imprint","IMPRINT",FACE,{"disambiguationData":[TD([[makeQuery(id+"F0.imprint","IMPRINT",EDGE,{"disambiguationData":[TD([[subQ2,1.0]])],"derivedFrom":subQ1}),-1.0]])]});}
            var Q3;
            {var subQ0=sQuery(id+"F0.wireOp",EDGE,"E14.left");var subQ1=sQuery(id+"F0.wireOp",EDGE,"E8");var subQ2=makeQuery(id+"F0.imprint","INTERSECT",VERTEX,{"disambiguationData":[OD(0.0)],"derivedFrom":[subQ1,subQ0]});Q3=makeQuery(id+"F0.imprint","IMPRINT",FACE,{"disambiguationData":[TD([[makeQuery(id+"F0.imprint","IMPRINT",EDGE,{"disambiguationData":[TD([[subQ2,1.0]])],"derivedFrom":subQ1}),1.0]])]});}
            var Q4;
            {var subQ0=sQuery(id+"F0.wireOp",EDGE,"E13.top");var subQ1=sQuery(id+"F0.wireOp",EDGE,"E9");var subQ2=makeQuery(id+"F0.imprint","INTERSECT",VERTEX,{"disambiguationData":[OD(0.0)],"derivedFrom":[subQ1,subQ0]});Q4=makeQuery(id+"F0.imprint","IMPRINT",FACE,{"disambiguationData":[TD([[makeQuery(id+"F0.imprint","IMPRINT",EDGE,{"disambiguationData":[TD([[subQ2,1.0]])],"derivedFrom":subQ1}),1.0]])]});}
            var Q5;
            {var subQ0=sQuery(id+"F0.wireOp",EDGE,"E9");var subQ1=sQuery(id+"F0.wireOp",EDGE,"E0");var subQ2=makeQuery(id+"F0.imprint","INTERSECT",VERTEX,{"disambiguationData":[OD(0.0)],"derivedFrom":[subQ1,subQ0]});Q5=makeQuery(id+"F0.imprint","IMPRINT",FACE,{"disambiguationData":[TD([[makeQuery(id+"F0.imprint","IMPRINT",EDGE,{"disambiguationData":[TD([[subQ2,-1.0]])],"derivedFrom":subQ1}),1.0]])]});}
            var Q6;
            {var subQ0=sQuery(id+"F0.wireOp",EDGE,"E13.top");var subQ1=sQuery(id+"F0.wireOp",EDGE,"E0");var subQ2=makeQuery(id+"F0.imprint","INTERSECT",VERTEX,{"derivedFrom":[subQ1,subQ0]});Q6=makeQuery(id+"F0.imprint","IMPRINT",FACE,{"disambiguationData":[TD([[makeQuery(id+"F0.imprint","IMPRINT",EDGE,{"disambiguationData":[TD([[subQ2,-1.0]])],"derivedFrom":subQ1}),-1.0]])]});}
            var Q7;
            {var subQ0=sQuery(id+"F0.wireOp",EDGE,"E9");var subQ1=sQuery(id+"F0.wireOp",EDGE,"E0");var subQ2=makeQuery(id+"F0.imprint","INTERSECT",VERTEX,{"disambiguationData":[OD(0.0)],"derivedFrom":[subQ1,subQ0]});Q7=makeQuery(id+"F0.imprint","IMPRINT",FACE,{"disambiguationData":[TD([[makeQuery(id+"F0.imprint","IMPRINT",EDGE,{"disambiguationData":[TD([[subQ2,-1.0]])],"derivedFrom":subQ1}),-1.0]])]});}
            extrude(context, id + "F9", {"entities" : qUnion([Q0, Q1, Q2, Q3, Q4, Q5, Q6, Q7]), "operationType" : NewBodyOperationType.ADD, "oppositeDirection" : true, "depth" : 3 * mm, "offsetDistance" : 25 * mm});
        }
        {
            var Q0;
            Q0=makeQuery(id+"F9.opExtrude","CAP_FACE",FACE,{"disambiguationData":[OSD([sQuery(id+"F0.wireOp",EDGE,"E9")])],"isStart":false});
            var Q1;
            Q1=makeQuery(id+"F9.opExtrude","CAP_FACE",FACE,{"disambiguationData":[OSD([sQuery(id+"F0.wireOp",EDGE,"E8")])],"isStart":false});
            chamfer(context, id + "F10", {"entities" : qUnion([Q0, Q1]), "width" : 2 * mm, "tangentPropagation" : true});
        }
        {
            var Q0;
            Q0=qCreatedBy(makeId("Front.planeOp"),FACE);
            var sketch = newSketch(context, id + "F11", { "sketchPlane" : qUnion([Q0])});
            skLineSegment(sketch, "E19", {"start": v(0, 0) * mm, "end": v(0, 25) * mm});
            skLineSegment(sketch, "E20.bottom", {"start": v(-19.86, 45) * mm, "end": v(19.86, 45) * mm});
            skLineSegment(sketch, "E20.top", {"start": v(-19.86, 5) * mm, "end": v(19.86, 5) * mm});
            skLineSegment(sketch, "E20.left", {"start": v(-19.86, 45) * mm, "end": v(-19.86, 5) * mm});
            skLineSegment(sketch, "E20.right", {"start": v(19.86, 45) * mm, "end": v(19.86, 5) * mm});
            skPoint(sketch, "E20.middle", {"position": v(0, 25) * mm});
            skSolve(sketch);
        }
        {
            var Q0;
            Q0 = qSketchRegion(id + "F11", true);
            extrude(context, id + "F12", {"entities" : qUnion([Q0]), "operationType" : NewBodyOperationType.INTERSECT, "endBound" : BoundingType.SYMMETRIC, "depth" : 40 * mm, "offsetDistance" : 25 * mm});
        }
    });
